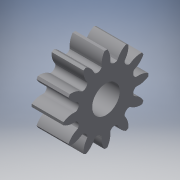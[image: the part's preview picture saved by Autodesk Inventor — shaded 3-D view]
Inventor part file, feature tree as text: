
AUTODESK INVENTOR PART (.ipt)
format: ipt  version: 2016 (Build 200138000, 138)  size: 275,456 bytes
history: native  units: in
note: dims shown in document units (in); Inventor stores cm internally (conversion verified against a paired STEP export)
features: extrude x3, sketch x3, plane x1
ambient origin geometry x8: Origin, YZ Plane, XZ Plane, XY Plane, X Axis, Y Axis, Z Axis, Center Point
bodies: Solid1 (feature_tree)
feature tree (7):
  plane  "Work Plane2"
  extrude  "Extrusion19"  Depth=0.2255in TaperAngle=0.0deg
  extrude  "Extrusion20"  Depth=100.0in TaperAngle=0.0deg
  extrude  "Extrusion21"  Depth=4.7244in TaperAngle=360.0deg
  sketch  "Sketch6"  dims[d92=4.7244in d94=360.0deg d102=0.2255in d103=0.0in]
  sketch  "Sketch7"  dims[d104=0.1949in d105=100.0in d106=0.0in]
  sketch  "Sketch8"  dims[d107=0.4in d108=4.7244in d110=360.0deg d112=100.0in d113=0.0in]
